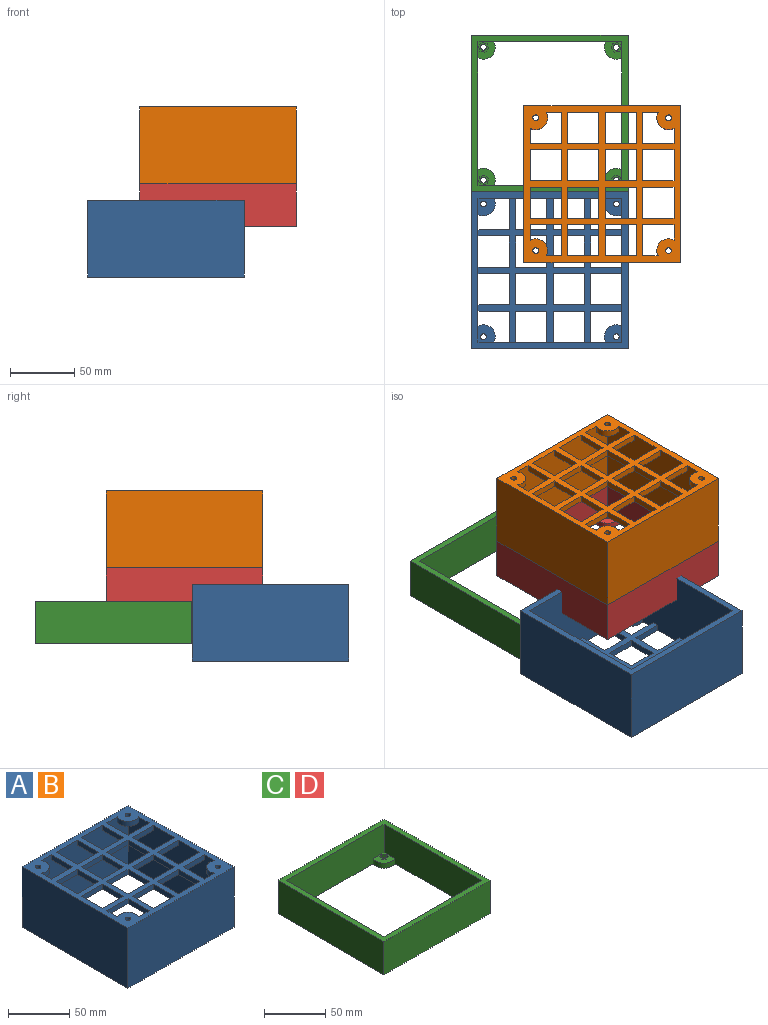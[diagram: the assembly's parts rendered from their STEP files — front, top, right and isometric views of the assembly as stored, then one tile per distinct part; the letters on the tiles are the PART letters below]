
ASSEMBLY  parts=4 mates=1
PART A: 71 faces, bbox 122x122x60 mm
  f0: plane 112x60mm, normal (1,0,0), area 6520.5mm2, adj f1,f3,f8,f9,f30,f31,f33,f34
  f1: plane 112x60mm, normal (0,1,0), area 6520.5mm2, adj f0,f2,f8,f9,f38,f39,f41,f42
  f2: plane 112x60mm, normal (-1,0,0), area 6520.5mm2, adj f1,f3,f8,f9,f46,f47,f49,f50
  f3: plane 112x60mm, normal (0,-1,0), area 6520.5mm2, adj f0,f2,f8,f9,f22,f23,f25,f26
  f4: plane 122x60mm, normal (0,-1,0), area 7320mm2, adj f5,f7,f8,f9
  f5: plane 122x60mm, normal (1,0,0), area 7320mm2, adj f4,f6,f8,f9
  f6: plane 122x60mm, normal (0,1,0), area 7320mm2, adj f5,f7,f8,f9
  f7: plane 122x60mm, normal (-1,0,0), area 7320mm2, adj f4,f6,f8,f9
  f8: plane 122x122mm, normal (0,0,1), area 6054.1mm2, adj f0,f1,f2,f3,f4,f5,f6,f7
  f9: plane 122x122mm, normal (0,0,-1), area 2340mm2, adj f0,f1,f2,f3,f4,f5,f6,f7
  f10: plane 24.25x5mm, normal (1,0,0), area 121.3mm2, adj f8,f11,f57,f58
  f11: plane 24.25x5mm, normal (0,-1,0), area 121.3mm2, adj f8,f10,f12,f58
  f12: plane 24.25x5mm, normal (-1,0,0), area 121.3mm2, adj f8,f11,f57,f58
  f13: plane 24.25x5mm, normal (1,0,0), area 121.3mm2, adj f8,f14,f53,f58
  f14: plane 24.25x5mm, normal (0,-1,0), area 121.3mm2, adj f8,f13,f15,f58
  f15: plane 24.25x5mm, normal (-1,0,0), area 121.3mm2, adj f8,f14,f53,f58
  f16: plane 24.25x5mm, normal (1,0,0), area 121.3mm2, adj f8,f17,f54,f58
  f17: plane 24.25x5mm, normal (0,-1,0), area 121.3mm2, adj f8,f16,f18,f58
  f18: plane 24.25x5mm, normal (-1,0,0), area 121.3mm2, adj f8,f17,f54,f58
  f19: plane 24.25x5mm, normal (1,0,0), area 121.3mm2, adj f8,f20,f55,f58
  f20: plane 24.25x5mm, normal (0,-1,0), area 121.3mm2, adj f8,f19,f21,f58
  f21: plane 24.25x5mm, normal (-1,0,0), area 121.3mm2, adj f8,f20,f55,f58
  f22: plane 24.25x5mm, normal (1,0,0), area 121.3mm2, adj f3,f8,f56,f58
  f23: plane 24.25x5mm, normal (-1,0,0), area 121.3mm2, adj f3,f8,f24,f58
  f24: plane 24.25x5mm, normal (0,1,0), area 121.3mm2, adj f8,f23,f25,f58
  f25: plane 24.25x5mm, normal (1,0,0), area 121.3mm2, adj f3,f8,f24,f58
  f26: plane 24.25x5mm, normal (-1,0,0), area 121.3mm2, adj f3,f8,f27,f58
  f27: plane 24.25x5mm, normal (0,1,0), area 121.3mm2, adj f8,f26,f28,f58
  f28: plane 24.25x5mm, normal (1,0,0), area 121.3mm2, adj f3,f8,f27,f58
  f29: plane 24.25x5mm, normal (-1,0,0), area 121.3mm2, adj f3,f8,f30,f58
  f30: plane 24.25x5mm, normal (0,1,0), area 121.3mm2, adj f0,f8,f29,f58
  f31: plane 24.25x5mm, normal (0,-1,0), area 121.3mm2, adj f0,f8,f32,f58
  f32: plane 24.25x5mm, normal (-1,0,0), area 121.3mm2, adj f8,f31,f33,f58
  f33: plane 24.25x5mm, normal (0,1,0), area 121.3mm2, adj f0,f8,f32,f58
  f34: plane 24.25x5mm, normal (0,-1,0), area 121.3mm2, adj f0,f8,f35,f58
  f35: plane 24.25x5mm, normal (-1,0,0), area 121.3mm2, adj f8,f34,f36,f58
  f36: plane 24.25x5mm, normal (0,1,0), area 121.3mm2, adj f0,f8,f35,f58
  f37: plane 24.25x5mm, normal (0,-1,0), area 121.3mm2, adj f0,f8,f38,f58
  f38: plane 24.25x5mm, normal (-1,0,0), area 121.3mm2, adj f1,f8,f37,f58
  f39: plane 24.25x5mm, normal (1,0,0), area 121.3mm2, adj f1,f8,f40,f58
  f40: plane 24.25x5mm, normal (0,-1,0), area 121.3mm2, adj f8,f39,f41,f58
  f41: plane 24.25x5mm, normal (-1,0,0), area 121.3mm2, adj f1,f8,f40,f58
  f42: plane 24.25x5mm, normal (1,0,0), area 121.3mm2, adj f1,f8,f43,f58
  f43: plane 24.25x5mm, normal (0,-1,0), area 121.3mm2, adj f8,f42,f44,f58
  f44: plane 24.25x5mm, normal (-1,0,0), area 121.3mm2, adj f1,f8,f43,f58
  f45: plane 24.25x5mm, normal (1,0,0), area 121.3mm2, adj f1,f8,f46,f58
  f46: plane 24.25x5mm, normal (0,-1,0), area 121.3mm2, adj f2,f8,f45,f58
  f47: plane 24.25x5mm, normal (0,1,0), area 121.3mm2, adj f2,f8,f48,f58
  f48: plane 24.25x5mm, normal (1,0,0), area 121.3mm2, adj f8,f47,f49,f58
  f49: plane 24.25x5mm, normal (0,-1,0), area 121.3mm2, adj f2,f8,f48,f58
  f50: plane 24.25x5mm, normal (0,1,0), area 121.3mm2, adj f2,f8,f51,f58
  f51: plane 24.25x5mm, normal (1,0,0), area 121.3mm2, adj f8,f50,f52,f58
  f52: plane 24.25x5mm, normal (0,-1,0), area 121.3mm2, adj f2,f8,f51,f58
  f53: plane 24.25x5mm, normal (0,1,0), area 121.3mm2, adj f8,f13,f15,f58
  f54: plane 24.25x5mm, normal (0,1,0), area 121.3mm2, adj f8,f16,f18,f58
  f55: plane 24.25x5mm, normal (0,1,0), area 121.3mm2, adj f8,f19,f21,f58
  f56: plane 24.25x5mm, normal (0,1,0), area 121.3mm2, adj f2,f8,f22,f58
  f57: plane 24.25x5mm, normal (0,1,0), area 121.3mm2, adj f8,f10,f12,f58
  f58: plane 112x112mm, normal (0,0,-1), area 3135mm2, adj f0,f1,f2,f3,f10,f11,f12,f13
  f59: cylinder r=9.24mm len=13.49mm, axis (0,0,1), area 116.7mm2, adj f2,f3,f8,f61
  f60: cylinder r=2.25mm len=5mm, axis (0,0,1), area 70.7mm2, adj f8,f61
  f61: plane 13.49x13.49mm, normal (0,0,-1), area 144.8mm2, adj f2,f3,f59,f60
  f62: cylinder r=9.24mm len=13.49mm, axis (0,0,1), area 116.7mm2, adj f1,f2,f8,f64
  f63: cylinder r=2.25mm len=5mm, axis (0,0,1), area 70.7mm2, adj f8,f64
  f64: plane 13.49x13.49mm, normal (0,0,-1), area 144.8mm2, adj f1,f2,f62,f63
  f65: cylinder r=9.24mm len=13.49mm, axis (0,0,1), area 116.7mm2, adj f0,f3,f8,f67
  f66: cylinder r=2.25mm len=5mm, axis (0,0,1), area 70.7mm2, adj f8,f67
  f67: plane 13.49x13.49mm, normal (0,0,-1), area 144.8mm2, adj f0,f3,f65,f66
  f68: cylinder r=9.24mm len=13.49mm, axis (0,0,1), area 116.7mm2, adj f0,f1,f8,f70
  f69: cylinder r=2.25mm len=5mm, axis (0,0,1), area 70.7mm2, adj f8,f70
  f70: plane 13.49x13.49mm, normal (0,0,-1), area 144.8mm2, adj f0,f1,f68,f69
PART B: same geometry as A
PART C: 50 faces, bbox 122x122x33 mm
  f0: cylinder r=2.25mm len=4.5mm, axis (0,0,-1), area 21.2mm2, adj f15,f43
  f1: cylinder r=2.25mm len=4.5mm, axis (0,0,-1), area 21.2mm2, adj f15,f42
  f2: plane 13.49x13.49mm, normal (0,0,1), area 119.1mm2, adj f7,f12,f18,f36,f37,f38,f39,f40
  f3: cylinder r=2.25mm len=4.5mm, axis (0,0,-1), area 21.2mm2, adj f15,f35
  f4: plane 13.49x13.49mm, normal (0,0,1), area 119.1mm2, adj f6,f11,f19,f29,f30,f31,f32,f33
  f5: cylinder r=2.25mm len=4.5mm, axis (0,0,-1), area 21.2mm2, adj f15,f22
  f6: plane 112x33mm, normal (0,1,0), area 3571.5mm2, adj f4,f7,f11,f14,f15,f19,f20,f21
  f7: plane 112x33mm, normal (1,0,0), area 3571.5mm2, adj f2,f6,f12,f14,f15,f18,f20,f21
  f8: plane 122x33mm, normal (0,-1,0), area 4026mm2, adj f9,f13,f14,f15
  f9: plane 122x33mm, normal (1,0,0), area 4026mm2, adj f8,f10,f14,f15
  f10: plane 122x33mm, normal (0,1,0), area 4026mm2, adj f9,f13,f14,f15
  f11: plane 112x33mm, normal (-1,0,0), area 3571.5mm2, adj f4,f6,f12,f14,f15,f16,f17,f19
  f12: plane 112x33mm, normal (0,-1,0), area 3571.5mm2, adj f2,f7,f11,f14,f15,f16,f17,f18
  f13: plane 122x33mm, normal (-1,0,0), area 4026mm2, adj f8,f10,f14,f15
  f14: plane 122x122mm, normal (0,0,1), area 2340mm2, adj f6,f7,f8,f9,f10,f11,f12,f13
  f15: plane 122x122mm, normal (0,0,-1), area 2919.1mm2, adj f0,f1,f3,f5,f6,f7,f8,f9
  f16: cylinder r=9.24mm len=13.49mm, axis (0,0,-1), area 116.7mm2, adj f11,f12,f15,f17
  f17: plane 13.49x13.49mm, normal (0,0,1), area 119.1mm2, adj f11,f12,f16,f44,f45,f46,f47,f48
  f18: cylinder r=9.24mm len=13.49mm, axis (0,0,-1), area 116.7mm2, adj f2,f7,f12,f15
  f19: cylinder r=9.24mm len=13.49mm, axis (0,0,-1), area 116.7mm2, adj f4,f6,f11,f15
  f20: cylinder r=9.24mm len=13.49mm, axis (0,0,-1), area 116.7mm2, adj f6,f7,f15,f21
  f21: plane 13.49x13.49mm, normal (0,0,1), area 119.1mm2, adj f6,f7,f20,f23,f24,f25,f26,f27
  f22: plane 7.74x7.71mm, normal (0,0,1), area 25.7mm2, adj f5,f23,f24,f25,f26,f27,f28
  f23: plane 3.5x2.85mm, normal (-0.71,-0.7,0), area 14mm2, adj f21,f22,f24,f28
  f24: plane 3.87x3.5mm, normal (0.25,-0.97,0), area 14mm2, adj f21,f22,f23,f25
  f25: plane 3.86x3.5mm, normal (0.96,-0.27,0), area 14mm2, adj f21,f22,f24,f26
  f26: plane 3.5x2.85mm, normal (0.71,0.7,0), area 14mm2, adj f21,f22,f25,f27
  f27: plane 3.87x3.5mm, normal (-0.25,0.97,0), area 14mm2, adj f21,f22,f26,f28
  f28: plane 3.86x3.5mm, normal (-0.96,0.27,0), area 14mm2, adj f21,f22,f23,f27
  f29: plane 3.86x3.5mm, normal (-0.96,-0.27,0), area 14mm2, adj f4,f30,f34,f35
  f30: plane 3.87x3.5mm, normal (-0.25,-0.97,0), area 14mm2, adj f4,f29,f31,f35
  f31: plane 3.5x2.85mm, normal (0.71,-0.7,0), area 14mm2, adj f4,f30,f32,f35
  f32: plane 3.86x3.5mm, normal (0.96,0.27,0), area 14mm2, adj f4,f31,f33,f35
  f33: plane 3.87x3.5mm, normal (0.25,0.97,0), area 14mm2, adj f4,f32,f34,f35
  f34: plane 3.5x2.85mm, normal (-0.71,0.7,0), area 14mm2, adj f4,f29,f33,f35
  f35: plane 7.74x7.71mm, normal (0,0,1), area 25.7mm2, adj f3,f29,f30,f31,f32,f33,f34
  f36: plane 3.86x3.5mm, normal (-0.96,-0.27,0), area 14mm2, adj f2,f37,f41,f42
  f37: plane 3.87x3.5mm, normal (-0.25,-0.97,0), area 14mm2, adj f2,f36,f38,f42
  f38: plane 3.5x2.85mm, normal (0.71,-0.7,0), area 14mm2, adj f2,f37,f39,f42
  f39: plane 3.86x3.5mm, normal (0.96,0.27,0), area 14mm2, adj f2,f38,f40,f42
  f40: plane 3.87x3.5mm, normal (0.25,0.97,0), area 14mm2, adj f2,f39,f41,f42
  f41: plane 3.5x2.85mm, normal (-0.71,0.7,0), area 14mm2, adj f2,f36,f40,f42
  f42: plane 7.74x7.71mm, normal (0,0,1), area 25.7mm2, adj f1,f36,f37,f38,f39,f40,f41
  f43: plane 7.74x7.71mm, normal (0,0,1), area 25.7mm2, adj f0,f44,f45,f46,f47,f48,f49
  f44: plane 3.5x2.85mm, normal (-0.71,-0.7,0), area 14mm2, adj f17,f43,f45,f49
  f45: plane 3.87x3.5mm, normal (0.25,-0.97,0), area 14mm2, adj f17,f43,f44,f46
  f46: plane 3.86x3.5mm, normal (0.96,-0.27,0), area 14mm2, adj f17,f43,f45,f47
  f47: plane 3.5x2.85mm, normal (0.71,0.7,0), area 14mm2, adj f17,f43,f46,f48
  f48: plane 3.87x3.5mm, normal (-0.25,0.97,0), area 14mm2, adj f17,f43,f47,f49
  f49: plane 3.86x3.5mm, normal (-0.96,0.27,0), area 14mm2, adj f17,f43,f44,f48
PART D: same geometry as C
PLACE A rot(axis=(-1,0,0),180deg) t=(-40.79,-76.93,293.43)mm
PLACE B at identity
PLACE C t=(-40.79,55.07,-26.07)mm
PLACE D at identity
MATE planar A.f4 <-> C.f8  axis (0,1,0) through (-40.79,-10.93,110.43)mm
